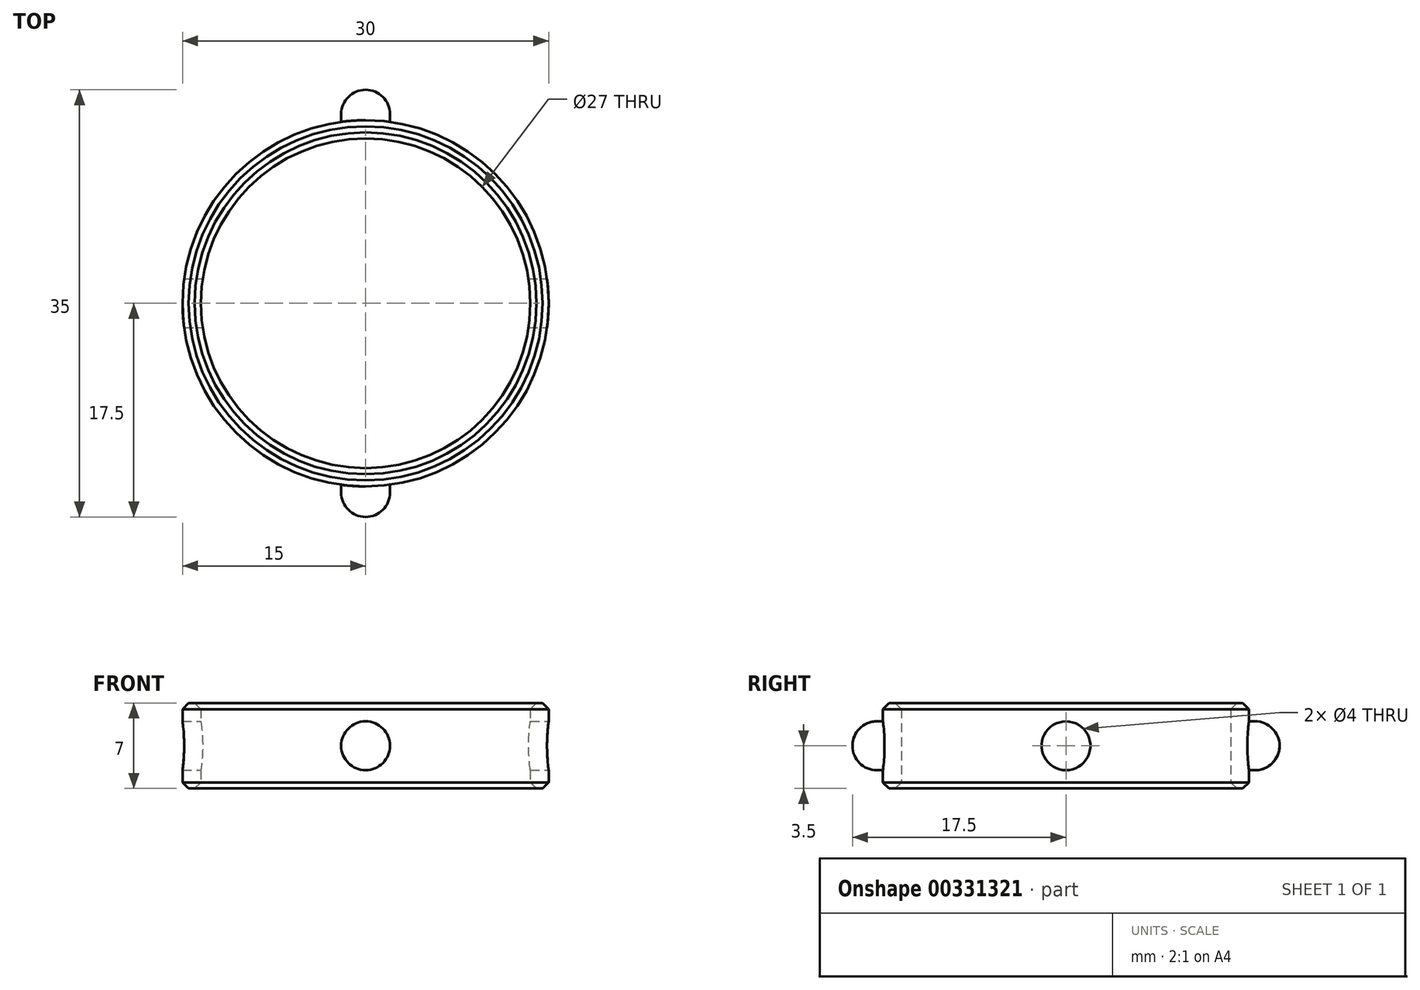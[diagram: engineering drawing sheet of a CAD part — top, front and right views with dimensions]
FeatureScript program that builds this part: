
annotation { "Feature Type Name" : "Feature", "Feature Type Description" : "" }
export const myFeature = defineFeature(function(context is Context, id is Id, definition is map)
    precondition{}
    {
        {
            var Q0;
            Q0=qCreatedBy(makeId("Top.planeOp"),FACE);
            var sketch = newSketch(context, id + "F0", { "sketchPlane" : qUnion([Q0])});
            skCircle(sketch, "E0", {"center": v(0, 0) * mm, "radius": 15 * mm});
            skCircle(sketch, "E1", {"center": v(0, 0) * mm, "radius": 13.5 * mm});
            skSolve(sketch);
        }
        {
            var Q0;
            Q0=makeQuery(id+"F0.imprint","IMPRINT",FACE,{"disambiguationData":[TD([[makeQuery(id+"F0.imprint","IMPRINT",EDGE,{"derivedFrom":sQuery(id+"F0.wireOp",EDGE,"E0")}),1.0]])]});
            extrude(context, id + "F1", {"entities" : qUnion([Q0]), "depth" : 7 * mm});
        }
        {
            var Q0;
            Q0=qCreatedBy(makeId("Right.planeOp"),FACE);
            var sketch = newSketch(context, id + "F2", { "sketchPlane" : qUnion([Q0])});
            skCircle(sketch, "E2", {"center": v(0, 3.5) * mm, "radius": 2 * mm});
            skLineSegment(sketch, "E3", {"start": v(0, 0) * mm, "end": v(0, 3.5) * mm, "construction": true});
            skLineSegment(sketch, "E4", {"start": v(0, 3.5) * mm, "end": v(0, 7) * mm, "construction": true});
            skSolve(sketch);
        }
        {
            var Q0;
            Q0=makeQuery(id+"F2.imprint","IMPRINT",FACE,{"disambiguationData":[TD([[makeQuery(id+"F2.imprint","IMPRINT",EDGE,{"derivedFrom":sQuery(id+"F2.wireOp",EDGE,"E2")}),1.0]])]});
            extrude(context, id + "F3", {"entities" : qUnion([Q0]), "operationType" : NewBodyOperationType.REMOVE, "endBound" : BoundingType.SYMMETRIC, "oppositeDirection" : true, "depth" : 40 * mm});
        }
        {
            var Q0;
            Q0=makeQuery(id+"F1.opExtrude","CAP_EDGE",EDGE,{"disambiguationData":[OSD([sQuery(id+"F0.wireOp",EDGE,"E0")])],"isStart":false});
            var Q1;
            Q1=makeQuery(id+"F1.opExtrude","CAP_EDGE",EDGE,{"disambiguationData":[OSD([sQuery(id+"F0.wireOp",EDGE,"E1")])],"isStart":false});
            var Q2;
            Q2=makeQuery(id+"F1.opExtrude","CAP_EDGE",EDGE,{"disambiguationData":[OSD([sQuery(id+"F0.wireOp",EDGE,"E0")])],"isStart":true});
            var Q3;
            Q3=makeQuery(id+"F1.opExtrude","CAP_EDGE",EDGE,{"disambiguationData":[OSD([sQuery(id+"F0.wireOp",EDGE,"E1")])],"isStart":true});
            chamfer(context, id + "F4", {"entities" : qUnion([Q0, Q1, Q2, Q3]), "width" : .5 * mm, "tangentPropagation" : true});
        }
        {
            var Q0;
            Q0=qCreatedBy(makeId("Front.planeOp"),FACE);
            cPlane(context, id + "F5", {"entities" : qUnion([Q0]), "cplaneType" : CPlaneType.OFFSET, "offset" : (27 / 2) * mm, "oppositeDirection" : true, "width" : 150 * mm, "height" : 150 * mm});
        }
        {
            var Q0;
            Q0=qCreatedBy(id+"F5.planeOp",FACE);
            var sketch = newSketch(context, id + "F6", { "sketchPlane" : qUnion([Q0])});
            skCircle(sketch, "E5", {"center": v(0, 3.5) * mm, "radius": 2 * mm});
            skLineSegment(sketch, "E6", {"start": v(0, 0) * mm, "end": v(0, 3.5) * mm, "construction": true});
            skLineSegment(sketch, "E7", {"start": v(0, 3.5) * mm, "end": v(0, 7) * mm, "construction": true});
            skSolve(sketch);
        }
        {
            var Q0;
            Q0 = qSketchRegion(id + "F6", true);
            extrude(context, id + "F7", {"entities" : qUnion([Q0]), "operationType" : NewBodyOperationType.ADD, "oppositeDirection" : true, "depth" : 4 * mm});
        }
        {
            var Q0;
            Q0=makeQuery(id+"F1.opExtrude","SWEPT_BODY",BODY,{"disambiguationData":[OSD([sQuery(id+"F0.wireOp",EDGE,"E0"),sQuery(id+"F0.wireOp",EDGE,"E1")])]});
            var Q1;
            Q1=qCreatedBy(makeId("Front.planeOp"),FACE);
            mirror(context, id + "F8", {"operationType" : NewBodyOperationType.ADD, "entities" : qUnion([Q0]), "mirrorPlane" : qUnion([Q1])});
        }
        {
            var Q0;
            Q0=makeQuery(id+"F8.opPattern","COPY",EDGE,{"derivedFrom":makeQuery(id+"F7.opExtrude","CAP_EDGE",EDGE,{"disambiguationData":[OSD([sQuery(id+"F6.wireOp",EDGE,"E5")])],"isStart":false}),"instanceName":"1"});
            var Q1;
            Q1=makeQuery(id+"F7.opExtrude","CAP_EDGE",EDGE,{"disambiguationData":[OSD([sQuery(id+"F6.wireOp",EDGE,"E5")])],"isStart":false});
            fillet(context, id + "F9", {"entities" : qUnion([Q0, Q1]), "radius" : 2 * mm, "tangentPropagation" : true, "allowEdgeOverflow" : false});
        }
    });
